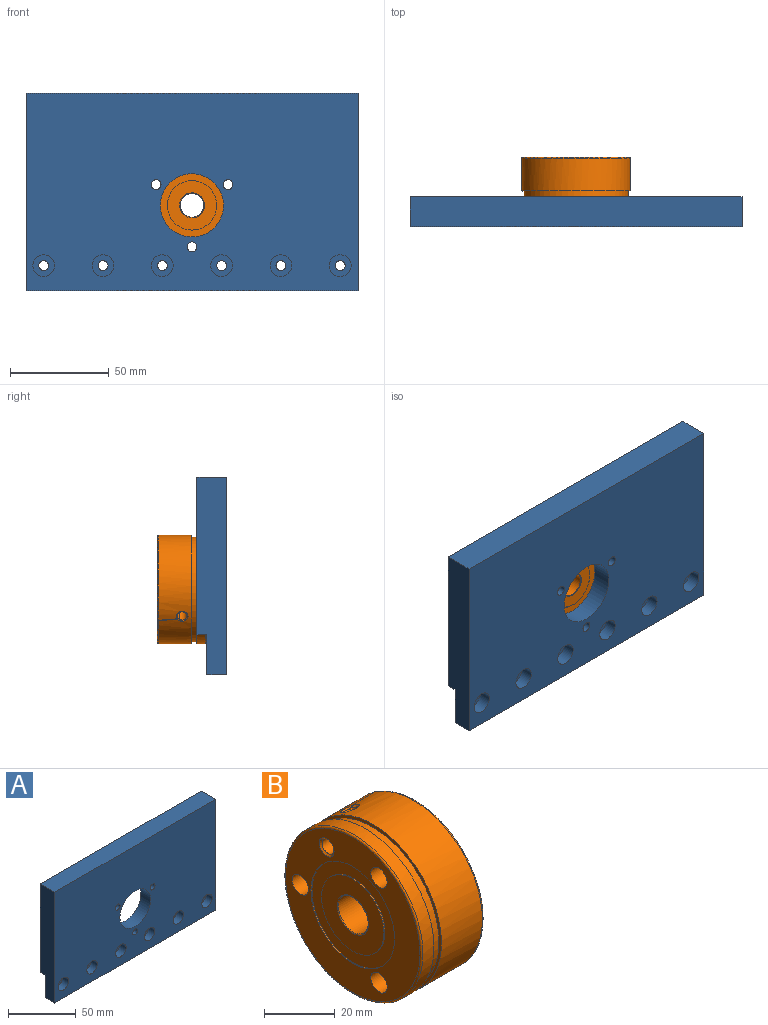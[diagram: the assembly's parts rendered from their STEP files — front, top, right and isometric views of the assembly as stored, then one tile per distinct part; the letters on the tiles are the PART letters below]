
ASSEMBLY  parts=2 mates=1
PART A: 32 faces, bbox 168x15x100.2 mm
  f0: cylinder r=2.5mm len=5mm, axis (0,1,0), area 55mm2, adj f19,f21
  f1: cylinder r=2.5mm len=5mm, axis (0,1,0), area 55mm2, adj f19,f25
  f2: cylinder r=2.5mm len=5mm, axis (0,1,0), area 55mm2, adj f19,f29
  f3: cylinder r=2.5mm len=5mm, axis (0,1,0), area 55mm2, adj f19,f31
  f4: cylinder r=2.5mm len=5mm, axis (0,1,0), area 55mm2, adj f19,f27
  f5: cylinder r=2.5mm len=5mm, axis (0,1,0), area 55mm2, adj f19,f23
  f6: plane 100.16x15mm, normal (1,0,0), area 1400.8mm2, adj f7,f9,f10,f15,f18,f19
  f7: plane 168x79.84mm, normal (0,1,0), area 11129.5mm2, adj f6,f8,f10,f16,f17,f18
  f8: plane 100.16x15mm, normal (-1,0,0), area 1400.8mm2, adj f7,f9,f10,f15,f17,f19
  f9: plane 168x10mm, normal (0,0,-1), area 1680mm2, adj f6,f8,f15,f19
  f10: plane 168x15mm, normal (0,0,1), area 2520mm2, adj f6,f7,f8,f15
  f11: cylinder r=2.5mm len=10mm, axis (0,1,0), area 157.1mm2, adj f15,f19
  f12: cylinder r=2.5mm len=10mm, axis (0,1,0), area 157.1mm2, adj f15,f19
  f13: cylinder r=2.5mm len=10mm, axis (0,1,0), area 157.1mm2, adj f15,f19
  f14: cylinder r=16mm len=32mm, axis (0,1,0), area 1005.3mm2, adj f15,f19
  f15: plane 168x100.16mm, normal (0,-1,0), area 15393.2mm2, adj f6,f8,f9,f10,f11,f12,f13,f14
  f16: cylinder r=27.5mm len=55mm, axis (0,1,0), area 704.4mm2, adj f7,f17,f18,f19
  f17: plane 68.93x5mm, normal (0,0,-1), area 344.6mm2, adj f7,f8,f16,f19
  f18: plane 68.93x5mm, normal (0,0,-1), area 344.6mm2, adj f6,f7,f16,f19
  f19: plane 168x70.82mm, normal (0,1,0), area 4716.1mm2, adj f0,f1,f2,f3,f4,f5,f6,f8
  f20: cylinder r=5.5mm len=11mm, axis (0,-1,0), area 224.6mm2, adj f15,f21
  f21: plane 11x11mm, normal (0,-1,0), area 75.4mm2, adj f0,f20
  f22: cylinder r=5.5mm len=11mm, axis (0,-1,0), area 224.6mm2, adj f15,f23
  f23: plane 11x11mm, normal (0,-1,0), area 75.4mm2, adj f5,f22
  f24: cylinder r=5.5mm len=11mm, axis (0,-1,0), area 224.6mm2, adj f15,f25
  f25: plane 11x11mm, normal (0,-1,0), area 75.4mm2, adj f1,f24
  f26: cylinder r=5.5mm len=11mm, axis (0,-1,0), area 224.6mm2, adj f15,f27
  f27: plane 11x11mm, normal (0,-1,0), area 75.4mm2, adj f4,f26
  f28: cylinder r=5.5mm len=11mm, axis (0,-1,0), area 224.6mm2, adj f15,f29
  f29: plane 11x11mm, normal (0,-1,0), area 75.4mm2, adj f2,f28
  f30: cylinder r=5.5mm len=11mm, axis (0,-1,0), area 224.6mm2, adj f15,f31
  f31: plane 11x11mm, normal (0,-1,0), area 75.4mm2, adj f3,f30
PART B: 49 faces, bbox 25x55x55 mm
  f0: cylinder r=16.75mm len=33.5mm, axis (1,0,0), area 457.8mm2, adj f1,f47
  f1: revolved ~33.5x33.5mm, area 637.8mm2, adj f0,f3
  f2: revolved ~33.5x33.5mm, area 637.8mm2, adj f3,f4
  f3: cylinder r=12.5mm len=25mm, axis (1,0,0), area 385.7mm2, adj f1,f2,f5
  f4: cylinder r=16.75mm len=33.5mm, axis (1,0,0), area 457.8mm2, adj f2,f48
  f5: cylinder r=1.5mm len=6.11mm, axis (0,-0.5,-0.87), area 50.1mm2, adj f3,f8
  f6: cone r=2.4mm half-angle=60deg, axis (-1,0,0), area 12.7mm2, adj f7,f9
  f7: cylinder r=2.4mm len=5.15mm, axis (-1,0,0), area 77.7mm2, adj f6,f10
  f8: cone r=2.4mm half-angle=60deg, axis (0,0.5,0.87), area 12.7mm2, adj f5,f16
  f9: cylinder r=1.5mm len=4.36mm, axis (1,0,0), area 38.5mm2, adj f6,f16
  f10: cone r=2.4mm half-angle=45deg, axis (-1,0,0), area 14.4mm2, adj f7,f14
  f11: revolved ~55x55mm, area 161.6mm2, adj f13,f14
  f12: cylinder r=16.75mm len=33.5mm, axis (1,0,0), area 42.1mm2, adj f14,f38
  f13: cylinder r=27.5mm len=55mm, axis (1,0,0), area 760.3mm2, adj f11,f15
  f14: plane 53.8x53.8mm, normal (-1,0,0), area 1258.7mm2, adj f10,f11,f12,f17,f18,f19
  f15: plane 55x55mm, normal (1,0,0), area 169.6mm2, adj f13,f21
  f16: cylinder r=2.4mm len=9.89mm, axis (0,0.5,0.87), area 123mm2, adj f8,f9,f22
  f17: cylinder r=3.25mm len=25mm, axis (1,0,0), area 510.5mm2, adj f14,f23
  f18: cylinder r=3.25mm len=25mm, axis (1,0,0), area 510.5mm2, adj f14,f23
  f19: cylinder r=3.25mm len=25mm, axis (1,0,0), area 510.5mm2, adj f14,f23
  f20: cylinder r=16.75mm len=33.5mm, axis (1,0,0), area 42.1mm2, adj f23,f37
  f21: cylinder r=26.5mm len=53mm, axis (1,0,0), area 499.5mm2, adj f15,f24
  f22: cone r=2.4mm half-angle=45deg, axis (0,0.5,0.87), area 12.2mm2, adj f16,f26
  f23: plane 53.8x53.8mm, normal (1,0,0), area 1286mm2, adj f17,f18,f19,f20,f25
  f24: plane 55x55mm, normal (-1,0,0), area 169.6mm2, adj f21,f26
  f25: revolved ~55x55mm, area 161.5mm2, adj f23,f26
  f26: cylinder r=27.5mm len=55mm, axis (1,0,0), area 2806.8mm2, adj f22,f24,f25
  f27: plane 25x25mm, normal (-1,0,0), area 366.1mm2, adj f28,f31
  f28: revolved ~12.6x12.6mm, area 18.1mm2, adj f27,f29
  f29: cylinder r=6mm len=12mm, axis (1,0,0), area 448.6mm2, adj f28,f30
  f30: revolved ~12.6x12.6mm, area 18.1mm2, adj f29,f35
  f31: cylinder r=12.5mm len=25mm, axis (1,0,0), area 31.4mm2, adj f27,f38
  f32: plane 25x25mm, normal (1,0,0), area 366.7mm2, adj f33,f36
  f33: revolved ~12.6x12.6mm, area 18.1mm2, adj f32,f34
  f34: cylinder r=6mm len=12mm, axis (-1,0,0), area 448.6mm2, adj f33,f35
  f35: revolved ~12.6x12.6mm, area 18.1mm2, adj f30,f34
  f36: cylinder r=12.5mm len=25mm, axis (-1,0,0), area 31.4mm2, adj f32,f37
  f37: plane 33.5x33.5mm, normal (1,0,0), area 390.5mm2, adj f20,f36
  f38: plane 33.5x33.5mm, normal (-1,0,0), area 390.5mm2, adj f12,f31
  f39: cone r=8.25mm half-angle=45deg, axis (1,0,0), area 21.6mm2, adj f40,f43
  f40: cylinder r=8.25mm len=16.5mm, axis (-1,0,0), area 334.3mm2, adj f39,f42
  f41: cylinder r=12.5mm len=25mm, axis (-1,0,0), area 7.9mm2, adj f42,f48
  f42: revolved ~25x25mm, area 410.8mm2, adj f40,f41
  f43: cone r=8.25mm half-angle=45deg, axis (-1,0,0), area 21.6mm2, adj f39,f44
  f44: cylinder r=8.25mm len=16.5mm, axis (1,0,0), area 334.3mm2, adj f43,f46
  f45: cylinder r=12.5mm len=25mm, axis (1,0,0), area 7.9mm2, adj f46,f47
  f46: revolved ~25x25mm, area 410.8mm2, adj f44,f45
  f47: plane 33.5x33.5mm, normal (1,0,0), area 390.5mm2, adj f0,f45
  f48: plane 33.5x33.5mm, normal (-1,0,0), area 390.5mm2, adj f4,f41
PLACE A t=(-35.68,-74.72,44.35)mm
PLACE B rot(axis=(-0.58,-0.58,0.58),120deg) t=(88.3,-79.72,-1.18)mm
MATE fastened B.f13 <-> A.f14  axis (0,-1,0) through (88.3,-79.72,-1.18)mm
